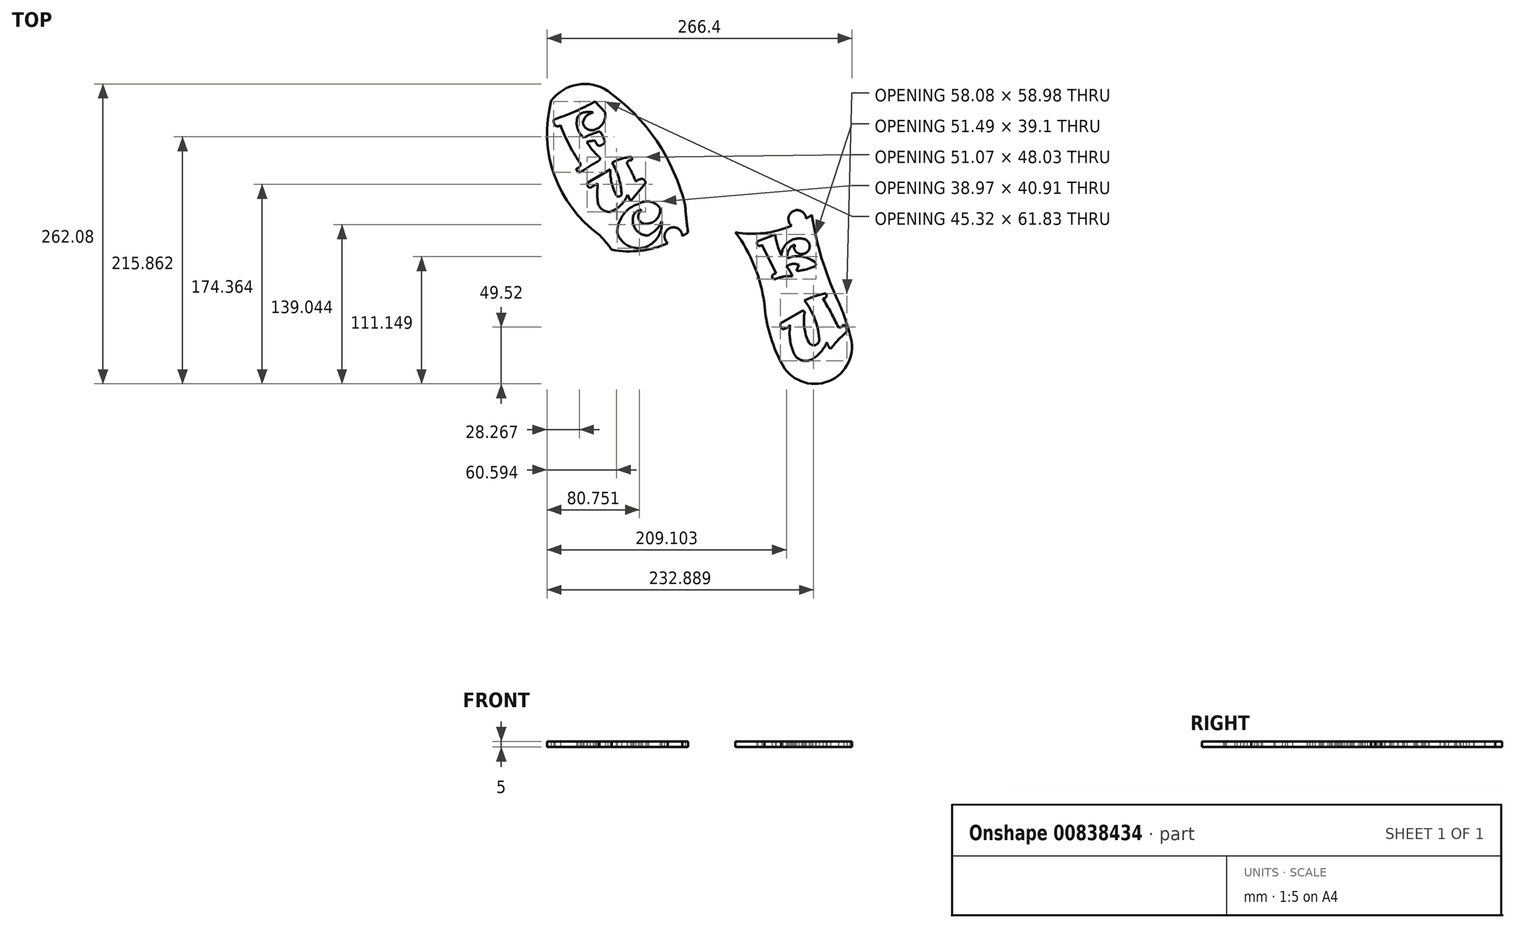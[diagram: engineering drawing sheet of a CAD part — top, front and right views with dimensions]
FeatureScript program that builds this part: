
annotation { "Feature Type Name" : "Feature", "Feature Type Description" : "" }
export const myFeature = defineFeature(function(context is Context, id is Id, definition is map)
    precondition{}
    {
        {
            var Q0;
            Q0=qCreatedBy(makeId("Top.planeOp"),FACE);
            var sketch = newSketch(context, id + "F0", { "sketchPlane" : qUnion([Q0])});
            skArc(sketch, "E0", {"start": v(-130.91, 85.24) * mm, "mid": v(-112.36, 92.25) * mm, "end": v(-94.6, 101.09) * mm});
            skArc(sketch, "E1", {"start": v(-130.91, 85.24) * mm, "mid": v(-130.6, 82.74) * mm, "end": v(-129.57, 80.44) * mm});
            skArc(sketch, "E2", {"start": v(-129.57, 80.44) * mm, "mid": v(-127.2, 79.35) * mm, "end": v(-124.85, 80.44) * mm});
            skArc(sketch, "E3", {"start": v(-124.85, 80.44) * mm, "mid": v(-116.92, 62.67) * mm, "end": v(-106.89, 46) * mm});
            skArc(sketch, "E4", {"start": v(-110.08, 42.64) * mm, "mid": v(-108.2, 44.05) * mm, "end": v(-106.89, 46) * mm});
            skArc(sketch, "E5", {"start": v(-110.08, 42.64) * mm, "mid": v(-110.85, 41.59) * mm, "end": v(-110.08, 40.54) * mm});
            skArc(sketch, "E6", {"start": v(-110.08, 40.54) * mm, "mid": v(-108.94, 39.55) * mm, "end": v(-107.45, 39.26) * mm});
            skArc(sketch, "E7", {"start": v(-91.82, 49) * mm, "mid": v(-99.7, 44.25) * mm, "end": v(-107.45, 39.26) * mm});
            skArc(sketch, "E8", {"start": v(-91.82, 49) * mm, "mid": v(-90.46, 50.3) * mm, "end": v(-90.48, 52.2) * mm});
            skArc(sketch, "E9", {"start": v(-101.77, 65.68) * mm, "mid": v(-96.64, 58.5) * mm, "end": v(-90.48, 52.2) * mm});
            skArc(sketch, "E10", {"start": v(-94.72, 66.68) * mm, "mid": v(-98.3, 66.56) * mm, "end": v(-101.77, 65.68) * mm});
            skArc(sketch, "E11", {"start": v(-94.72, 66.68) * mm, "mid": v(-93.3, 64.27) * mm, "end": v(-91.43, 62.18) * mm});
            skArc(sketch, "E12", {"start": v(-91.43, 62.18) * mm, "mid": v(-88.26, 63.37) * mm, "end": v(-85.79, 65.68) * mm});
            skArc(sketch, "E13", {"start": v(-85.79, 65.68) * mm, "mid": v(-87.69, 70.59) * mm, "end": v(-90.48, 75.04) * mm});
            skArc(sketch, "E14", {"start": v(-90.48, 75.04) * mm, "mid": v(-97.5, 72.6) * mm, "end": v(-104.28, 69.5) * mm});
            skArc(sketch, "E15", {"start": v(-109.68, 87.79) * mm, "mid": v(-109.97, 77.76) * mm, "end": v(-104.28, 69.5) * mm});
            skArc(sketch, "E16", {"start": v(-104.28, 91.51) * mm, "mid": v(-107.4, 90.26) * mm, "end": v(-109.68, 87.79) * mm});
            skArc(sketch, "E17", {"start": v(-96.21, 91.51) * mm, "mid": v(-100.25, 91.93) * mm, "end": v(-104.28, 91.51) * mm});
            skArc(sketch, "E18", {"start": v(-96.21, 91.51) * mm, "mid": v(-102.17, 88.4) * mm, "end": v(-105.28, 82.45) * mm});
            skArc(sketch, "E19", {"start": v(-105.28, 82.45) * mm, "mid": v(-100.77, 76.75) * mm, "end": v(-93.5, 76.94) * mm});
            skArc(sketch, "E20", {"start": v(-93.5, 76.94) * mm, "mid": v(-87.16, 82.91) * mm, "end": v(-85.79, 91.51) * mm});
            skLineSegment(sketch, "E21", {"start": v(-85.79, 91.51) * mm, "end": v(-94.6, 101.09) * mm});
            skArc(sketch, "E22", {"start": v(-81.32, 41.85) * mm, "mid": v(-80.14, 30.26) * mm, "end": v(-76.1, 19.32) * mm});
            skArc(sketch, "E23", {"start": v(-76.1, 19.32) * mm, "mid": v(-72.91, 18.26) * mm, "end": v(-71.54, 21.34) * mm});
            skArc(sketch, "E24", {"start": v(-71.54, 21.34) * mm, "mid": v(-74.07, 35) * mm, "end": v(-79.72, 47.7) * mm});
            skArc(sketch, "E25", {"start": v(-63.36, 52.7) * mm, "mid": v(-71.76, 50.93) * mm, "end": v(-79.72, 47.7) * mm});
            skArc(sketch, "E26", {"start": v(-63.36, 49.5) * mm, "mid": v(-62.24, 51.1) * mm, "end": v(-63.36, 52.7) * mm});
            skArc(sketch, "E27", {"start": v(-63.36, 49.5) * mm, "mid": v(-65.92, 48.83) * mm, "end": v(-66.33, 46.2) * mm});
            skArc(sketch, "E28", {"start": v(-59.1, 31.12) * mm, "mid": v(-62.36, 38.84) * mm, "end": v(-66.33, 46.2) * mm});
            skArc(sketch, "E29", {"start": v(-53.16, 33.46) * mm, "mid": v(-56.35, 32.84) * mm, "end": v(-59.1, 31.12) * mm});
            skArc(sketch, "E30", {"start": v(-50.4, 29.74) * mm, "mid": v(-51.23, 32) * mm, "end": v(-53.16, 33.46) * mm});
            skLineSegment(sketch, "E31", {"start": v(-50.4, 29.74) * mm, "end": v(-63.36, 14.22) * mm});
            skLineSegment(sketch, "E32", {"start": v(-63.36, 14.22) * mm, "end": v(-66.23, 19.64) * mm});
            skArc(sketch, "E33", {"start": v(-81.21, 4.66) * mm, "mid": v(-72.07, 10.5) * mm, "end": v(-66.23, 19.64) * mm});
            skArc(sketch, "E34", {"start": v(-92.32, 14.05) * mm, "mid": v(-88.7, 7.06) * mm, "end": v(-81.21, 4.66) * mm});
            skArc(sketch, "E35", {"start": v(-92.26, 29.52) * mm, "mid": v(-92.41, 27.36) * mm, "end": v(-92.5, 25.18) * mm});
            skArc(sketch, "E36", {"start": v(-92.5, 25.18) * mm, "mid": v(-92.66, 19.35) * mm, "end": v(-92.26, 13.53) * mm});
            skPoint(sketch, "E37.orphan", {"position": v(-92.26, 16.35) * mm});
            skLineSegment(sketch, "E38", {"start": v(-92.26, 29.52) * mm, "end": v(-99.16, 25.62) * mm});
            skArc(sketch, "E39", {"start": v(-101.34, 29.92) * mm, "mid": v(-101.08, 27.35) * mm, "end": v(-99.16, 25.62) * mm});
            skLineSegment(sketch, "E40", {"start": v(-101.34, 29.92) * mm, "end": v(-81.32, 41.85) * mm});
            skArc(sketch, "E41", {"start": v(-54.5, 5.6) * mm, "mid": v(-55.8, -2.78) * mm, "end": v(-47.8, -5.53) * mm});
            skArc(sketch, "E42", {"start": v(-47.8, -5.53) * mm, "mid": v(-40.07, -0.89) * mm, "end": v(-37.88, 7.85) * mm});
            skArc(sketch, "E43", {"start": v(-37.88, 7.85) * mm, "mid": v(-46.29, 13.52) * mm, "end": v(-56.27, 11.72) * mm});
            skArc(sketch, "E44", {"start": v(-75.25, -13.57) * mm, "mid": v(-62.75, -26.2) * mm, "end": v(-45.2, -23.38) * mm});
            skArc(sketch, "E45", {"start": v(-56.27, 11.72) * mm, "mid": v(-69.95, 2.22) * mm, "end": v(-75.25, -13.57) * mm});
            skArc(sketch, "E46", {"start": v(-45.2, -23.38) * mm, "mid": v(-38.16, -14.6) * mm, "end": v(-36.39, -3.5) * mm});
            skArc(sketch, "E47", {"start": v(-48.8, -16.04) * mm, "mid": v(-41.24, -11.1) * mm, "end": v(-36.39, -3.5) * mm});
            skArc(sketch, "E48", {"start": v(-60.54, 2.5) * mm, "mid": v(-59.6, -9.9) * mm, "end": v(-48.8, -16.04) * mm});
            skArc(sketch, "E49", {"start": v(-54.5, 6.5) * mm, "mid": v(-57.88, 5.05) * mm, "end": v(-60.54, 2.5) * mm});
            skArc(sketch, "E50", {"start": v(-54.5, 5.6) * mm, "mid": v(-54.4, 6.04) * mm, "end": v(-54.5, 6.5) * mm});
            skArc(sketch, "E51", {"start": v(-20.57, -34.32) * mm, "mid": v(-33.52, -37.07) * mm, "end": v(-39.76, -48.75) * mm});
            skArc(sketch, "E52", {"start": v(-22.2, -47.5) * mm, "mid": v(-15.15, -41.68) * mm, "end": v(-20.57, -34.32) * mm});
            skArc(sketch, "E53", {"start": v(-28.85, -41.48) * mm, "mid": v(-26.78, -45.87) * mm, "end": v(-22.2, -47.5) * mm});
            skArc(sketch, "E54", {"start": v(-28.85, -41.48) * mm, "mid": v(-27.83, -40.5) * mm, "end": v(-28.85, -39.54) * mm});
            skArc(sketch, "E55", {"start": v(-28.85, -39.54) * mm, "mid": v(-33.58, -44.46) * mm, "end": v(-34.4, -51.24) * mm});
            skArc(sketch, "E56", {"start": v(-45.2, -30.35) * mm, "mid": v(-43.27, -39.78) * mm, "end": v(-39.76, -48.75) * mm});
            skLineSegment(sketch, "E57", {"start": v(-45.2, -30.35) * mm, "end": v(-60.63, -36.46) * mm});
            skArc(sketch, "E58", {"start": v(-60.63, -36.46) * mm, "mid": v(-60.26, -39.97) * mm, "end": v(-56.77, -39.45) * mm});
            skLineSegment(sketch, "E59", {"start": v(-56.77, -39.45) * mm, "end": v(-44.54, -64.53) * mm});
            skArc(sketch, "E60", {"start": v(-44.54, -64.53) * mm, "mid": v(-46.69, -65.3) * mm, "end": v(-48.03, -67.15) * mm});
            skArc(sketch, "E61", {"start": v(-48.03, -67.15) * mm, "mid": v(-46.75, -69.17) * mm, "end": v(-44.36, -69.08) * mm});
            skArc(sketch, "E62", {"start": v(-30.27, -67.15) * mm, "mid": v(-35.99, -67.02) * mm, "end": v(-41.6, -68.2) * mm});
            skArc(sketch, "E63", {"start": v(-30.27, -67.15) * mm, "mid": v(-32.32, -62.48) * mm, "end": v(-35.48, -58.48) * mm});
            skArc(sketch, "E64", {"start": v(-24.5, -57.2) * mm, "mid": v(-30.18, -56.24) * mm, "end": v(-35.48, -58.48) * mm});
            skLineSegment(sketch, "E65", {"start": v(-24.5, -57.2) * mm, "end": v(-26.74, -62.19) * mm});
            skArc(sketch, "E66", {"start": v(-10.29, -55.02) * mm, "mid": v(-21.82, -49.78) * mm, "end": v(-34.4, -51.24) * mm});
            skArc(sketch, "E67", {"start": v(-12.48, -58.85) * mm, "mid": v(-10, -57.73) * mm, "end": v(-10.29, -55.02) * mm});
            skArc(sketch, "E68", {"start": v(-26.74, -62.19) * mm, "mid": v(-19.42, -61.34) * mm, "end": v(-12.48, -58.85) * mm});
            skArc(sketch, "E69", {"start": v(-132.9, 101.66) * mm, "mid": v(-130.09, 36.65) * mm, "end": v(-90.98, -15.37) * mm});
            skArc(sketch, "E70", {"start": v(-83.53, 110.35) * mm, "mid": v(-109.94, 115.84) * mm, "end": v(-132.9, 101.66) * mm});
            skArc(sketch, "E71", {"start": v(-15.86, 10.4) * mm, "mid": v(-40.74, 66.44) * mm, "end": v(-83.53, 110.35) * mm});
            skArc(sketch, "E72", {"start": v(-15.86, 10.4) * mm, "mid": v(-7.93, -39.37) * mm, "end": v(9, -86.84) * mm});
            skArc(sketch, "E73", {"start": v(20.08, -118.01) * mm, "mid": v(15.2, -102.19) * mm, "end": v(9, -86.84) * mm});
            skArc(sketch, "E74", {"start": v(-40.03, -142.3) * mm, "mid": v(1.55, -158.67) * mm, "end": v(20.08, -118.01) * mm});
            skArc(sketch, "E75", {"start": v(-54.7, -90.8) * mm, "mid": v(-50, -117.3) * mm, "end": v(-40.03, -142.3) * mm});
            skArc(sketch, "E76", {"start": v(-54.7, -90.8) * mm, "mid": v(-66.86, -50.21) * mm, "end": v(-90.98, -15.37) * mm});
            skArc(sketch, "E77", {"start": v(-19.45, -98.24) * mm, "mid": v(-19.8, -111.9) * mm, "end": v(-15.76, -124.96) * mm});
            skArc(sketch, "E78", {"start": v(-15.76, -124.96) * mm, "mid": v(-9.94, -127.02) * mm, "end": v(-6.72, -121.75) * mm});
            skArc(sketch, "E79", {"start": v(-6.72, -121.75) * mm, "mid": v(-10.78, -104.1) * mm, "end": v(-19.59, -88.28) * mm});
            skArc(sketch, "E80", {"start": v(-19.45, -98.24) * mm, "mid": v(-20.62, -97.3) * mm, "end": v(-22.1, -97.53) * mm});
            skArc(sketch, "E81", {"start": v(-40.57, -108.31) * mm, "mid": v(-40.35, -111.2) * mm, "end": v(-38.4, -113.33) * mm});
            skLineSegment(sketch, "E82", {"start": v(-40.57, -108.31) * mm, "end": v(-22.1, -97.53) * mm});
            skArc(sketch, "E83", {"start": v(-38.4, -113.33) * mm, "mid": v(-34.87, -112) * mm, "end": v(-32.12, -109.41) * mm});
            skArc(sketch, "E84", {"start": v(-32.12, -109.41) * mm, "mid": v(-32.4, -121.09) * mm, "end": v(-29.67, -132.44) * mm});
            skArc(sketch, "E85", {"start": v(-29.67, -132.44) * mm, "mid": v(-23.2, -140.06) * mm, "end": v(-13.2, -139.67) * mm});
            skArc(sketch, "E86", {"start": v(-13.2, -139.67) * mm, "mid": v(-5.43, -133.2) * mm, "end": v(0, -124.65) * mm});
            skArc(sketch, "E87", {"start": v(0, -124.65) * mm, "mid": v(1.09, -127.8) * mm, "end": v(3.15, -130.44) * mm});
            skArc(sketch, "E88", {"start": v(17.28, -115.3) * mm, "mid": v(9.96, -122.63) * mm, "end": v(3.15, -130.44) * mm});
            skArc(sketch, "E89", {"start": v(17.28, -115.3) * mm, "mid": v(16.85, -111.8) * mm, "end": v(14.5, -109.19) * mm});
            skArc(sketch, "E90", {"start": v(10.03, -111.8) * mm, "mid": v(12.73, -111.3) * mm, "end": v(14.5, -109.19) * mm});
            skPoint(sketch, "E90.startSnap0", {"position": v(16.85, -111.8) * mm});
            skArc(sketch, "E91", {"start": v(10.03, -111.8) * mm, "mid": v(3.58, -98.85) * mm, "end": v(-3.66, -86.33) * mm});
            skArc(sketch, "E92", {"start": v(-3.66, -86.33) * mm, "mid": v(-0.73, -85.17) * mm, "end": v(-1.05, -82.03) * mm});
            skArc(sketch, "E93", {"start": v(-1.05, -82.03) * mm, "mid": v(-10.56, -84.44) * mm, "end": v(-19.59, -88.28) * mm});
            skLineSegment(sketch, "E94", {"start": v(-44.36, -69.08) * mm, "end": v(-41.6, -68.2) * mm});
            skPoint(sketch, "E95.orphan", {"position": v(-43.9, -69.08) * mm});
            skArc(sketch, "E96", {"start": v(-79.94, -28.5) * mm, "mid": v(-55.02, -29.34) * mm, "end": v(-30.98, -22.74) * mm});
            skArc(sketch, "E97", {"start": v(-18.27, -16.54) * mm, "mid": v(-15.73, -15.03) * mm, "end": v(-13.24, -13.45) * mm});
            skArc(sketch, "E98", {"start": v(-18.27, -16.54) * mm, "mid": v(-29.49, -9.67) * mm, "end": v(-30.98, -22.74) * mm});
            skSolve(sketch);
        }
        {
            var Q0;
            Q0=makeQuery(id+"F0.imprint","IMPRINT",FACE,{"disambiguationData":[TD([[makeQuery(id+"F0.imprint","IMPRINT",EDGE,{"derivedFrom":sQuery(id+"F0.wireOp",EDGE,"E0")}),1.0]])]});
            extrude(context, id + "F1", {"entities" : qUnion([Q0]), "depth" : 5 * mm, "offsetDistance" : 25 * mm});
        }
        {
            var Q0;
            Q0=qCreatedBy(makeId("Top.planeOp"),FACE);
            var sketch = newSketch(context, id + "F2", { "sketchPlane" : qUnion([Q0])});
            skArc(sketch, "E99", {"start": v(87.47, -18.97) * mm, "mid": v(74.51, -21.72) * mm, "end": v(68.27, -33.4) * mm});
            skArc(sketch, "E100", {"start": v(85.84, -32.15) * mm, "mid": v(92.89, -26.33) * mm, "end": v(87.47, -18.97) * mm});
            skArc(sketch, "E101", {"start": v(79.19, -26.12) * mm, "mid": v(81.26, -30.52) * mm, "end": v(85.84, -32.15) * mm});
            skArc(sketch, "E102", {"start": v(79.19, -26.12) * mm, "mid": v(80.2, -25.16) * mm, "end": v(79.19, -24.19) * mm});
            skArc(sketch, "E103", {"start": v(79.19, -24.19) * mm, "mid": v(74.45, -29.11) * mm, "end": v(73.63, -35.9) * mm});
            skArc(sketch, "E104", {"start": v(62.84, -15) * mm, "mid": v(64.77, -24.43) * mm, "end": v(68.27, -33.4) * mm});
            skLineSegment(sketch, "E105", {"start": v(62.84, -15) * mm, "end": v(47.4, -21.1) * mm});
            skArc(sketch, "E106", {"start": v(47.4, -21.1) * mm, "mid": v(47.78, -24.62) * mm, "end": v(51.27, -24.1) * mm});
            skLineSegment(sketch, "E107", {"start": v(51.27, -24.1) * mm, "end": v(63.5, -49.17) * mm});
            skArc(sketch, "E108", {"start": v(63.5, -49.17) * mm, "mid": v(61.34, -49.94) * mm, "end": v(60, -51.8) * mm});
            skArc(sketch, "E109", {"start": v(60, -51.8) * mm, "mid": v(61.28, -53.81) * mm, "end": v(63.67, -53.73) * mm});
            skArc(sketch, "E110", {"start": v(77.77, -51.8) * mm, "mid": v(72.04, -51.66) * mm, "end": v(66.44, -52.84) * mm});
            skArc(sketch, "E111", {"start": v(77.77, -51.8) * mm, "mid": v(75.72, -47.13) * mm, "end": v(72.55, -43.13) * mm});
            skArc(sketch, "E112", {"start": v(83.54, -41.84) * mm, "mid": v(77.86, -40.88) * mm, "end": v(72.55, -43.13) * mm});
            skLineSegment(sketch, "E113", {"start": v(83.54, -41.84) * mm, "end": v(81.3, -46.83) * mm});
            skArc(sketch, "E114", {"start": v(97.74, -39.67) * mm, "mid": v(86.21, -34.43) * mm, "end": v(73.63, -35.9) * mm});
            skArc(sketch, "E115", {"start": v(95.55, -43.5) * mm, "mid": v(98.03, -42.38) * mm, "end": v(97.74, -39.67) * mm});
            skArc(sketch, "E116", {"start": v(81.3, -46.83) * mm, "mid": v(88.62, -45.98) * mm, "end": v(95.55, -43.5) * mm});
            skArc(sketch, "E117", {"start": v(94.8, 1.9) * mm, "mid": v(103.33, -35.57) * mm, "end": v(117.02, -71.5) * mm});
            skArc(sketch, "E118", {"start": v(128.11, -102.66) * mm, "mid": v(123.24, -86.83) * mm, "end": v(117.02, -71.5) * mm});
            skArc(sketch, "E119", {"start": v(68, -126.95) * mm, "mid": v(109.58, -143.32) * mm, "end": v(128.11, -102.66) * mm});
            skArc(sketch, "E120", {"start": v(53.33, -75.45) * mm, "mid": v(58.04, -101.95) * mm, "end": v(68, -126.95) * mm});
            skArc(sketch, "E121", {"start": v(53.33, -75.45) * mm, "mid": v(44.65, -42.7) * mm, "end": v(28.1, -13.14) * mm});
            skArc(sketch, "E122", {"start": v(88.58, -82.89) * mm, "mid": v(88.24, -96.55) * mm, "end": v(92.27, -109.6) * mm});
            skArc(sketch, "E123", {"start": v(92.27, -109.6) * mm, "mid": v(98.1, -111.67) * mm, "end": v(101.31, -106.4) * mm});
            skArc(sketch, "E124", {"start": v(101.31, -106.4) * mm, "mid": v(97.25, -88.75) * mm, "end": v(88.45, -72.92) * mm});
            skArc(sketch, "E125", {"start": v(88.58, -82.89) * mm, "mid": v(87.42, -81.95) * mm, "end": v(85.94, -82.18) * mm});
            skArc(sketch, "E126", {"start": v(67.46, -92.96) * mm, "mid": v(67.68, -95.84) * mm, "end": v(69.64, -97.97) * mm});
            skLineSegment(sketch, "E127", {"start": v(67.46, -92.96) * mm, "end": v(85.94, -82.18) * mm});
            skArc(sketch, "E128", {"start": v(69.64, -97.97) * mm, "mid": v(73.16, -96.64) * mm, "end": v(75.92, -94.06) * mm});
            skArc(sketch, "E129", {"start": v(75.92, -94.06) * mm, "mid": v(75.63, -105.73) * mm, "end": v(78.37, -117.09) * mm});
            skArc(sketch, "E130", {"start": v(78.37, -117.09) * mm, "mid": v(84.84, -124.7) * mm, "end": v(94.83, -124.32) * mm});
            skArc(sketch, "E131", {"start": v(94.83, -124.32) * mm, "mid": v(102.6, -117.84) * mm, "end": v(108.03, -109.3) * mm});
            skArc(sketch, "E132", {"start": v(108.03, -109.3) * mm, "mid": v(109.12, -112.46) * mm, "end": v(111.18, -115.08) * mm});
            skArc(sketch, "E133", {"start": v(125.31, -99.95) * mm, "mid": v(118, -107.28) * mm, "end": v(111.18, -115.08) * mm});
            skArc(sketch, "E134", {"start": v(125.31, -99.95) * mm, "mid": v(124.89, -96.45) * mm, "end": v(122.53, -93.84) * mm});
            skArc(sketch, "E135", {"start": v(118.06, -96.45) * mm, "mid": v(120.77, -95.95) * mm, "end": v(122.53, -93.84) * mm});
            skPoint(sketch, "E135.startSnap0", {"position": v(124.89, -96.45) * mm});
            skArc(sketch, "E136", {"start": v(118.06, -96.45) * mm, "mid": v(111.62, -83.5) * mm, "end": v(104.37, -70.98) * mm});
            skArc(sketch, "E137", {"start": v(104.37, -70.98) * mm, "mid": v(107.3, -69.82) * mm, "end": v(106.99, -66.68) * mm});
            skArc(sketch, "E138", {"start": v(106.99, -66.68) * mm, "mid": v(97.48, -69.1) * mm, "end": v(88.45, -72.92) * mm});
            skLineSegment(sketch, "E139", {"start": v(63.67, -53.73) * mm, "end": v(66.44, -52.84) * mm});
            skPoint(sketch, "E140.orphan", {"position": v(64.14, -53.73) * mm});
            skArc(sketch, "E141", {"start": v(28.1, -13.14) * mm, "mid": v(53.01, -13.98) * mm, "end": v(77.05, -7.38) * mm});
            skArc(sketch, "E142", {"start": v(89.76, -1.18) * mm, "mid": v(92.3, 0.32) * mm, "end": v(94.8, 1.9) * mm});
            skPoint(sketch, "E143.end.orphan", {"position": v(62.84, -8.03) * mm});
            skArc(sketch, "E144", {"start": v(89.76, -1.18) * mm, "mid": v(78.7, 5.38) * mm, "end": v(77.05, -7.38) * mm});
            skSolve(sketch);
        }
        {
            var Q0;
            Q0=makeQuery(id+"F2.imprint","IMPRINT",FACE,{"disambiguationData":[TD([[makeQuery(id+"F2.imprint","IMPRINT",EDGE,{"derivedFrom":sQuery(id+"F2.wireOp",EDGE,"E99")}),-1.0]])]});
            extrude(context, id + "F3", {"entities" : qUnion([Q0]), "depth" : 5 * mm, "offsetDistance" : 25 * mm});
        }
    });
